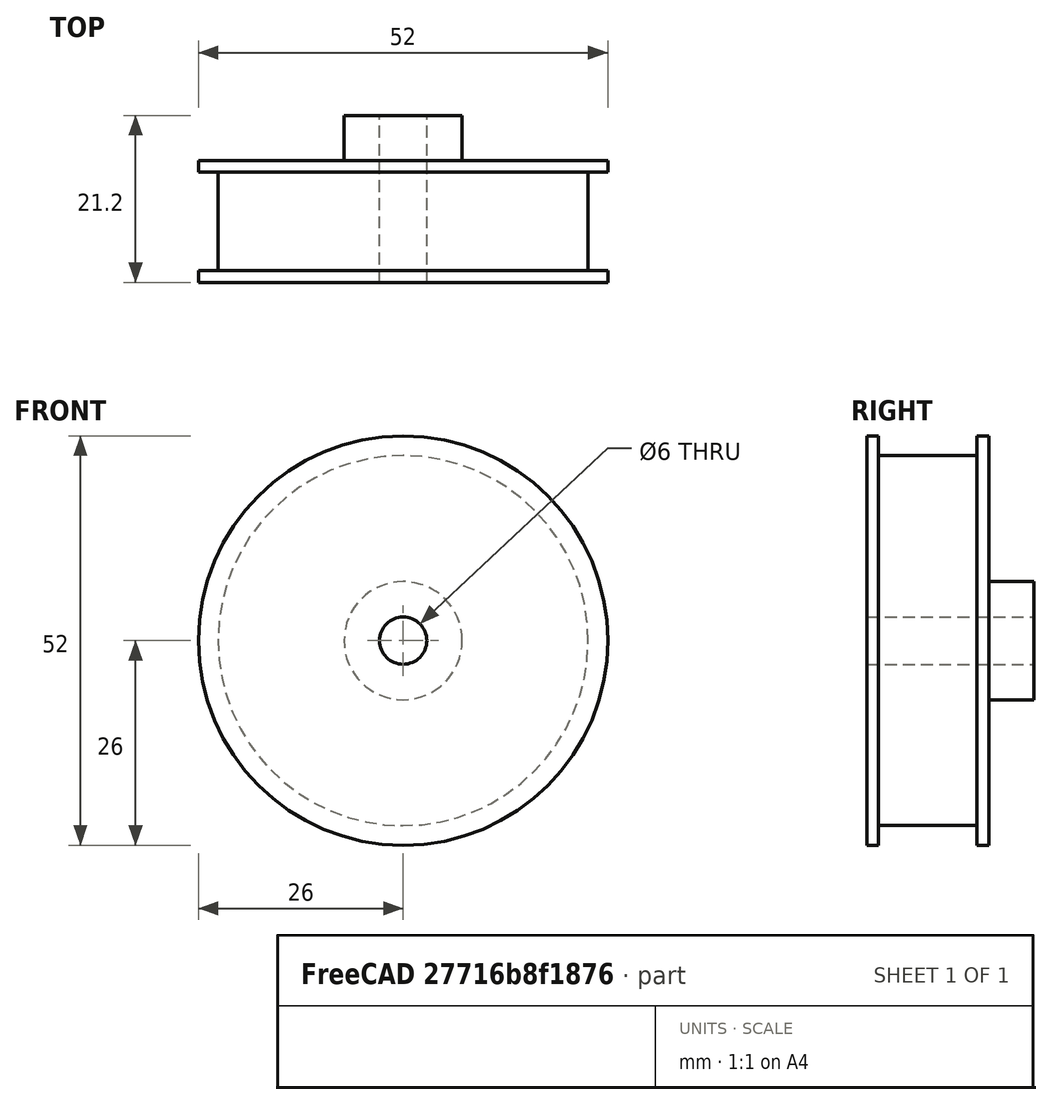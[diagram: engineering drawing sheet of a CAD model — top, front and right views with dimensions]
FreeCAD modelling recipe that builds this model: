
FCSTD DOCUMENT  (FreeCAD 0.15R4669 (Git))
Label: BR_grandePoulie
License: All rights reserved
LicenseURL: http://en.wikipedia.org/wiki/All_rights_reserved
objects: Sketcher::SketchObject×1, Part::Revolution×1
note: 2 computed .brp shape members not serialized (recipe doc carries the construction recipe); baked Part::Feature solids carry a one-line shape summary decoded from their .brp

FEATURE [Sketcher::SketchObject] Sketch  label="coupeGrandePoulie"
  sketch-geometry (10):
    g0: LineSegment StartX=3 StartY=-10.6 StartZ=0 EndX=3 EndY=10.6 EndZ=0
    g1: LineSegment StartX=3 StartY=10.6 StartZ=0 EndX=7.5 EndY=10.6 EndZ=0
    g2: LineSegment StartX=7.5 StartY=10.6 StartZ=0 EndX=7.5 EndY=4.9 EndZ=0
    g3: LineSegment StartX=7.5 StartY=4.9 StartZ=0 EndX=26 EndY=4.9 EndZ=0
    g4: LineSegment StartX=26 StartY=4.9 StartZ=0 EndX=26 EndY=3.4 EndZ=0
    g5: LineSegment StartX=26 StartY=3.4 StartZ=0 EndX=23.5 EndY=3.4 EndZ=0
    g6: LineSegment StartX=23.5 StartY=3.4 StartZ=0 EndX=23.5 EndY=-9.1 EndZ=0
    g7: LineSegment StartX=23.5 StartY=-9.1 StartZ=0 EndX=26 EndY=-9.1 EndZ=0
    g8: LineSegment StartX=26 StartY=-9.1 StartZ=0 EndX=26 EndY=-10.6 EndZ=0
    g9: LineSegment StartX=26 StartY=-10.6 StartZ=0 EndX=3 EndY=-10.6 EndZ=0
  constraints (30):
    c: Vertical(g0)
    c: Coincident(g1,g0)
    c: Horizontal(g1)
    c: Coincident(g2,g1)
    c: Vertical(g2)
    c: Coincident(g3,g2)
    c: Horizontal(g3)
    c: Coincident(g4,g3)
    c: Vertical(g4)
    c: Coincident(g5,g4)
    c: Horizontal(g5)
    c: Coincident(g6,g5)
    c: Vertical(g6)
    c: Coincident(g7,g6)
    c: Horizontal(g7)
    c: Coincident(g8,g7)
    c: Vertical(g8)
    c: Coincident(g9,g8)
    c: Coincident(g9,g0)
    c: Horizontal(g9)
    c: PointOnObject(g4,g8)
    c: DistanceX(g-1,g0) = 3
    c: DistanceX(g-1,g1) = 7.5
    c: DistanceY(g3,g8) = -15.5
    c: DistanceY(g0,g0) = 21.2
    c: Symmetric(g0,g0,g-1)
    c: DistanceY(g6) = -12.5
    c: DistanceX(g-1,g5) = 23.5
    c: DistanceX(g-1,g8) = 26
    c: DistanceY(g8) = -1.5
FEATURE [Part::Revolution] Revolve  label="grandePoulie"
  Angle = 360
  Axis = (0,1,0)
  Base = (0,0,0)
  Solid = true
  Source = -> Sketch
